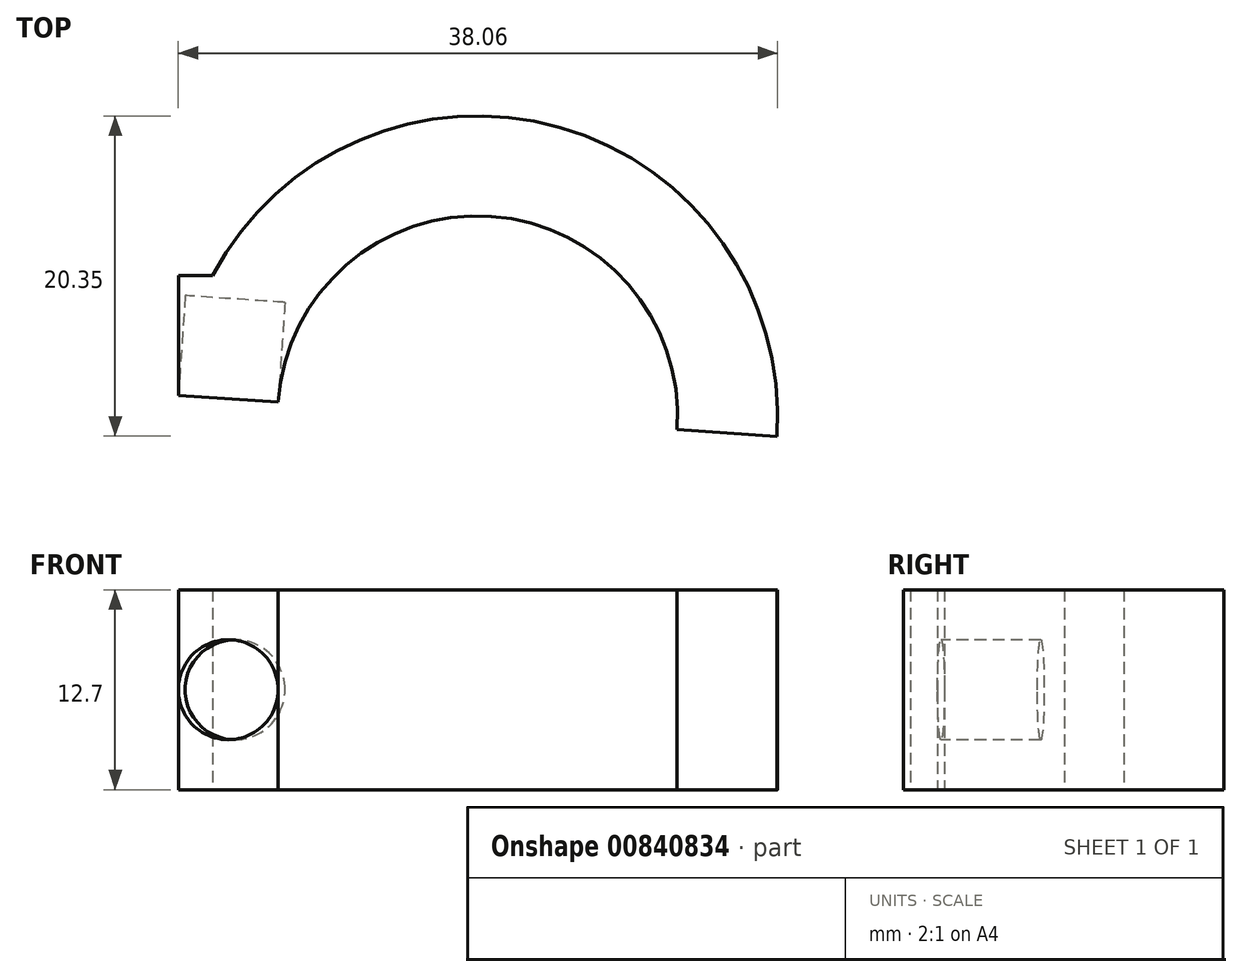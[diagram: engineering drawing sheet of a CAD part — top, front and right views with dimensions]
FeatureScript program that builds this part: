
annotation { "Feature Type Name" : "Feature", "Feature Type Description" : "" }
export const myFeature = defineFeature(function(context is Context, id is Id, definition is map)
    precondition{}
    {
        {
            var Q0;
            Q0=qCreatedBy(makeId("Top.planeOp"),FACE);
            var sketch = newSketch(context, id + "F0", { "sketchPlane" : qUnion([Q0])});
            skLineSegment(sketch, "E0.top", {"start": v(-12.7, -42.14) * mm, "end": v(0, -42.14) * mm});
            skLineSegment(sketch, "E0.left", {"start": v(-12.7, 34.06) * mm, "end": v(-12.7, -42.14) * mm});
            skLineSegment(sketch, "E0.right", {"start": v(0, 34.06) * mm, "end": v(0, -42.14) * mm});
            skLineSegment(sketch, "E1", {"start": v(0, -42.14) * mm, "end": v(-6.35, -42.14) * mm});
            skCircle(sketch, "E2", {"center": v(-6.35, -42.14) * mm, "radius": 12.7 * mm});
            skPoint(sketch, "E3.oppositeSnap0", {"position": v(-12.7, 40.4) * mm});
            skCircle(sketch, "E4", {"center": v(-6.35, 40.4) * mm, "radius": 12.7 * mm});
            skCircle(sketch, "E5", {"center": v(-6.35, 40.4) * mm, "radius": 19.05 * mm});
            skLineSegment(sketch, "E6", {"start": v(-6.35, 40.4) * mm, "end": v(-25.36, 41.7) * mm});
            skLineSegment(sketch, "E7", {"start": v(-6.35, 40.4) * mm, "end": v(12.66, 39.1) * mm});
            skLineSegment(sketch, "E8.bottom", {"start": v(-25.36, 41.7) * mm, "end": v(-19, 41.7) * mm});
            skLineSegment(sketch, "E8.top", {"start": v(-25.36, 49.33) * mm, "end": v(-19, 49.33) * mm});
            skLineSegment(sketch, "E8.left", {"start": v(-25.36, 41.7) * mm, "end": v(-25.36, 49.33) * mm});
            skLineSegment(sketch, "E8.right", {"start": v(-19, 41.7) * mm, "end": v(-19, 49.33) * mm});
            skLineSegment(sketch, "E9.bottom", {"start": v(0, 0) * mm, "end": v(-12.7, 0) * mm});
            skLineSegment(sketch, "E9.top", {"start": v(0, -12.7) * mm, "end": v(-12.7, -12.7) * mm});
            skLineSegment(sketch, "E9.left", {"start": v(0, 0) * mm, "end": v(0, -12.7) * mm});
            skLineSegment(sketch, "E9.right", {"start": v(-12.7, 0) * mm, "end": v(-12.7, -12.7) * mm});
            skLineSegment(sketch, "E10.left", {"start": v(-12.7, -12.7) * mm, "end": v(-12.7, 0) * mm});
            skLineSegment(sketch, "E11.right", {"start": v(0, 0) * mm, "end": v(0, -42.14) * mm});
            skLineSegment(sketch, "E12.bottom", {"start": v(25.4, -42.14) * mm, "end": v(12.7, -42.14) * mm});
            skArc(sketch, "E13", {"start": v(12.7, -42.14) * mm, "mid": v(9.46, -20.14) * mm, "end": v(0, 0) * mm});
            skArc(sketch, "E14", {"start": v(25.4, -42.14) * mm, "mid": v(22.16, -20.14) * mm, "end": v(12.7, 0) * mm});
            skArc(sketch, "E15", {"start": v(12.7, 0) * mm, "mid": v(5.65, 21.24) * mm, "end": v(-12.7, 34.06) * mm});
            skSolve(sketch);
        }
        {
            var Q0;
            {var subQ0=sQuery(id+"F0.wireOp",EDGE,"E8.bottom");Q0=makeQuery(id+"F0.imprint","IMPRINT",FACE,{"disambiguationData":[TD([[makeQuery(id+"F0.imprint","IMPRINT",EDGE,{"derivedFrom":subQ0}),-1.0]])]});}
            var Q1;
            {var subQ0=sQuery(id+"F0.wireOp",EDGE,"E8.bottom");Q1=makeQuery(id+"F0.imprint","IMPRINT",FACE,{"disambiguationData":[TD([[makeQuery(id+"F0.imprint","IMPRINT",EDGE,{"derivedFrom":subQ0}),1.0]])]});}
            var Q2;
            {var subQ0=sQuery(id+"F0.wireOp",EDGE,"E8.left");Q2=makeQuery(id+"F0.imprint","IMPRINT",FACE,{"disambiguationData":[TD([[makeQuery(id+"F0.imprint","IMPRINT",EDGE,{"derivedFrom":subQ0}),-1.0]])]});}
            extrude(context, id + "F1", {"entities" : qUnion([Q0, Q1, Q2]), "depth" : 12.7 * mm, "offsetDistance" : 25.4 * mm});
        }
        {
            var Q0;
            Q0=makeQuery(id+"F1.opExtrude","SWEPT_FACE",FACE,{"disambiguationData":[OSD([sQuery(id+"F0.wireOp",EDGE,"E6")])]});
            var sketch = newSketch(context, id + "F2", { "sketchPlane" : qUnion([Q0])});
            skLineSegment(sketch, "E16.bottom", {"start": v(-28.14, 12.7) * mm, "end": v(-24.97, 12.7) * mm});
            skLineSegment(sketch, "E16.left", {"start": v(-28.14, 12.7) * mm, "end": v(-28.14, 6.35) * mm});
            skCircle(sketch, "E17", {"center": v(-24.97, 6.35) * mm, "radius": 3.18 * mm});
            skSolve(sketch);
        }
        {
            var Q0;
            {var subQ0=sQuery(id+"F2.wireOp",EDGE,"E17");var subQ1=sQuery(id+"F0.wireOp",EDGE,"E6");var subQ3=makeQuery(id+"F2.imprint","INTERSECT",VERTEX,{"derivedFrom":[makeQuery(id+"F1.opExtrude","SWEPT_EDGE",EDGE,{"disambiguationData":[OSD([sQuery(id+"F0.wireOp",EDGE,"E4"),subQ1])]}),subQ0]});Q0=makeQuery(id+"F2.imprint","IMPRINT",FACE,{"disambiguationData":[TD([[makeQuery(id+"F2.imprint","IMPRINT",EDGE,{"disambiguationData":[TD([[subQ3,-1.0]])],"derivedFrom":subQ0}),1.0]])]});}
            extrude(context, id + "F3", {"entities" : qUnion([Q0]), "operationType" : NewBodyOperationType.REMOVE, "oppositeDirection" : true, "depth" : 6.35 * mm, "offsetDistance" : 25.4 * mm});
        }
    });
